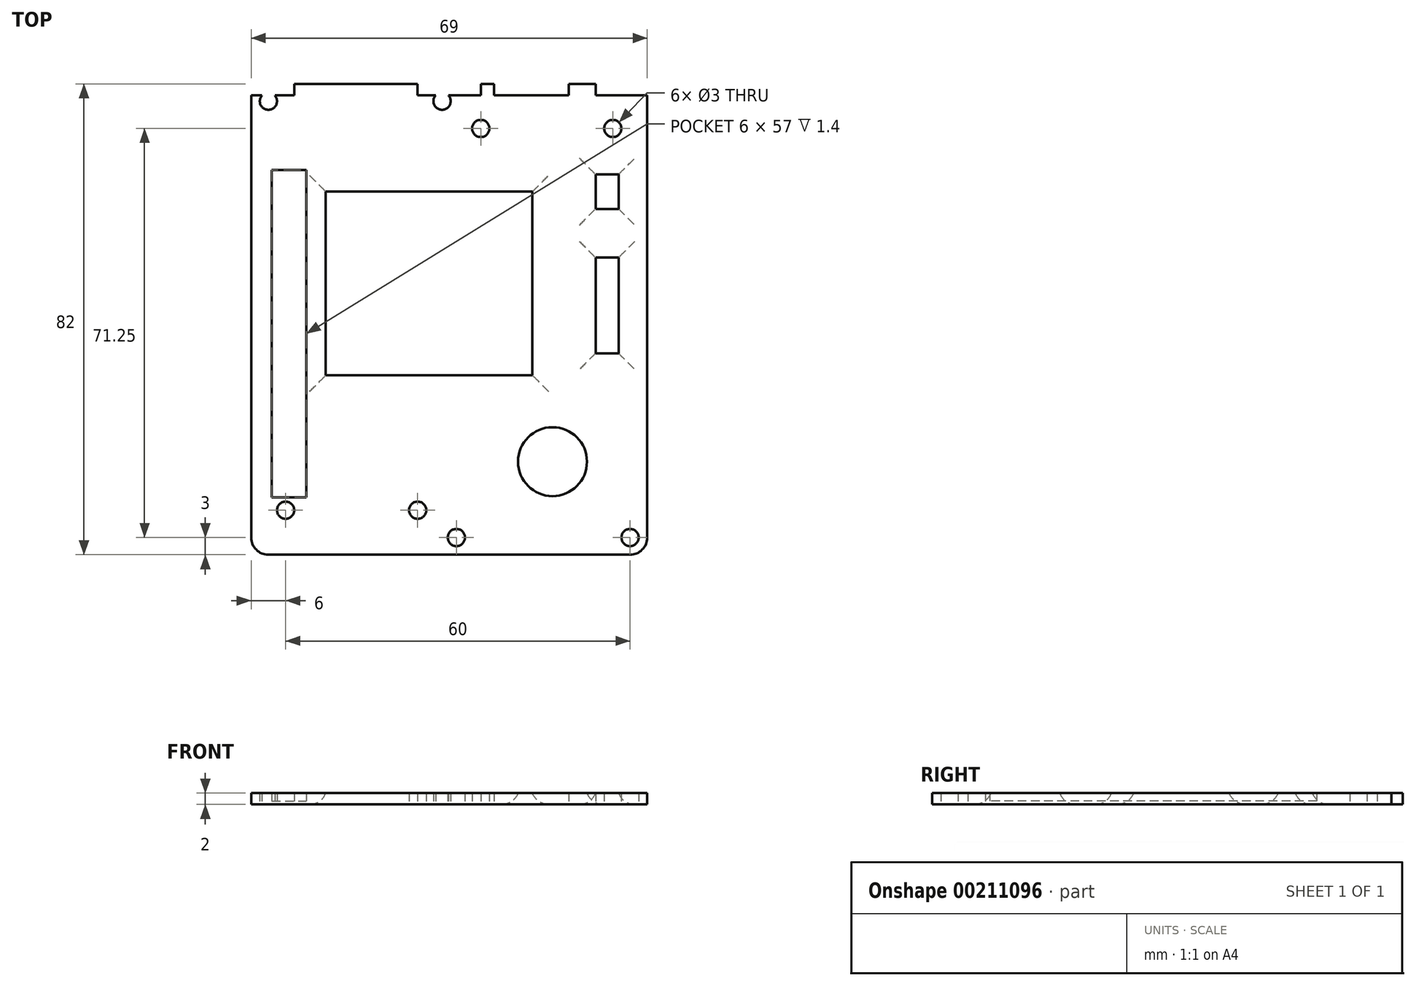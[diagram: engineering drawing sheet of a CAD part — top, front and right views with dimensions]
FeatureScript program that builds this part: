
annotation { "Feature Type Name" : "Feature", "Feature Type Description" : "" }
export const myFeature = defineFeature(function(context is Context, id is Id, definition is map)
    precondition{}
    {
        {
            var Q0;
            Q0=qCreatedBy(makeId("Top.planeOp"),FACE);
            var sketch = newSketch(context, id + "F0", { "sketchPlane" : qUnion([Q0])});
            skLineSegment(sketch, "E0.bottom", {"start": v(34.5, -41) * mm, "end": v(-34.5, -41) * mm});
            skLineSegment(sketch, "E0.top", {"start": v(34.5, 41) * mm, "end": v(-34.5, 41) * mm});
            skLineSegment(sketch, "E0.left", {"start": v(34.5, -41) * mm, "end": v(34.5, 41) * mm});
            skLineSegment(sketch, "E0.right", {"start": v(-34.5, -41) * mm, "end": v(-34.5, 41) * mm});
            skPoint(sketch, "E0.middle", {"position": v(0, 0) * mm});
            skLineSegment(sketch, "E1", {"start": v(-34.5, 39) * mm, "end": v(34.5, 39) * mm});
            skCircle(sketch, "E2", {"center": v(-28.5, 33.25) * mm, "radius": 1.5 * mm});
            skCircle(sketch, "E3", {"center": v(-5.5, 33.25) * mm, "radius": 1.5 * mm});
            skCircle(sketch, "E4.MirrorC", {"center": v(5.5, 33.25) * mm, "radius": 1.5 * mm});
            skCircle(sketch, "E5.MirrorC", {"center": v(28.5, 33.25) * mm, "radius": 1.5 * mm});
            skLineSegment(sketch, "E6.bottom", {"start": v(-21.5, 22.25) * mm, "end": v(14.5, 22.25) * mm});
            skLineSegment(sketch, "E6.top", {"start": v(-21.5, -9.75) * mm, "end": v(14.5, -9.75) * mm});
            skLineSegment(sketch, "E6.left", {"start": v(-21.5, 22.25) * mm, "end": v(-21.5, -9.75) * mm});
            skLineSegment(sketch, "E6.right", {"start": v(14.5, 22.25) * mm, "end": v(14.5, -9.75) * mm});
            skLineSegment(sketch, "E7.bottom", {"start": v(25.5, 25.25) * mm, "end": v(29.5, 25.25) * mm});
            skLineSegment(sketch, "E7.top", {"start": v(25.5, 19.25) * mm, "end": v(29.5, 19.25) * mm});
            skLineSegment(sketch, "E7.left", {"start": v(25.5, 25.25) * mm, "end": v(25.5, 19.25) * mm});
            skLineSegment(sketch, "E7.right", {"start": v(29.5, 25.25) * mm, "end": v(29.5, 19.25) * mm});
            skLineSegment(sketch, "E8.bottom", {"start": v(29.5, 10.75) * mm, "end": v(25.5, 10.75) * mm});
            skLineSegment(sketch, "E8.top", {"start": v(29.5, -5.91) * mm, "end": v(25.5, -5.91) * mm});
            skLineSegment(sketch, "E8.left", {"start": v(29.5, 10.75) * mm, "end": v(29.5, -5.91) * mm});
            skLineSegment(sketch, "E8.right", {"start": v(25.5, 10.75) * mm, "end": v(25.5, -5.91) * mm});
            skLineSegment(sketch, "E9.bottom", {"start": v(-5.5, 41) * mm, "end": v(5.5, 41) * mm});
            skLineSegment(sketch, "E9.top", {"start": v(-5.5, 39) * mm, "end": v(5.5, 39) * mm});
            skLineSegment(sketch, "E9.left", {"start": v(-5.5, 41) * mm, "end": v(-5.5, 39) * mm});
            skLineSegment(sketch, "E9.right", {"start": v(5.5, 41) * mm, "end": v(5.5, 39) * mm});
            skLineSegment(sketch, "E10.bottom", {"start": v(28.5, 39) * mm, "end": v(34.5, 39) * mm});
            skLineSegment(sketch, "E10.top", {"start": v(28, 41) * mm, "end": v(34.5, 41) * mm});
            skLineSegment(sketch, "E10.right", {"start": v(34.5, 39) * mm, "end": v(34.5, 41) * mm});
            skLineSegment(sketch, "E11.bottom", {"start": v(-28.5, 39) * mm, "end": v(-34.5, 39) * mm});
            skLineSegment(sketch, "E11.top", {"start": v(-27, 41) * mm, "end": v(-34.5, 41) * mm});
            skLineSegment(sketch, "E11.right", {"start": v(-34.5, 39) * mm, "end": v(-34.5, 41) * mm});
            skLineSegment(sketch, "E12", {"start": v(-25.5, 41) * mm, "end": v(-25.5, 39) * mm});
            skLineSegment(sketch, "E13.MirrorCS", {"start": v(25.5, 41) * mm, "end": v(25.5, 39) * mm});
            skLineSegment(sketch, "E14.bottom", {"start": v(-37, 41) * mm, "end": v(37, 41) * mm});
            skLineSegment(sketch, "E14.top", {"start": v(-37, -43.29) * mm, "end": v(37, -43.29) * mm});
            skLineSegment(sketch, "E14.left", {"start": v(-37, 41) * mm, "end": v(-37, -43.29) * mm});
            skLineSegment(sketch, "E14.right", {"start": v(37, 41) * mm, "end": v(37, -43.29) * mm});
            skLineSegment(sketch, "E15.bottom", {"start": v(-10.5, -43.29) * mm, "end": v(10.5, -43.29) * mm});
            skLineSegment(sketch, "E15.top", {"start": v(-10.5, -51.29) * mm, "end": v(10.5, -51.29) * mm});
            skLineSegment(sketch, "E15.left", {"start": v(-10.5, -43.29) * mm, "end": v(-10.5, -51.29) * mm});
            skLineSegment(sketch, "E15.right", {"start": v(10.5, -43.29) * mm, "end": v(10.5, -51.29) * mm});
            skLineSegment(sketch, "E16.bottom", {"start": v(-12.5, -41) * mm, "end": v(12.5, -41) * mm});
            skLineSegment(sketch, "E16.top", {"start": v(-12.5, -53.5) * mm, "end": v(12.5, -53.5) * mm});
            skLineSegment(sketch, "E16.left", {"start": v(-12.5, -41) * mm, "end": v(-12.5, -53.5) * mm});
            skLineSegment(sketch, "E16.right", {"start": v(12.5, -41) * mm, "end": v(12.5, -53.5) * mm});
            skLineSegment(sketch, "E17", {"start": v(-10.5, -43.29) * mm, "end": v(-10.5, -41) * mm});
            skLineSegment(sketch, "E18.MirrorCS", {"start": v(10.5, -43.29) * mm, "end": v(10.5, -41) * mm});
            skLineSegment(sketch, "E19.bottom", {"start": v(20.8, 41) * mm, "end": v(7.8, 41) * mm});
            skLineSegment(sketch, "E19.top", {"start": v(20.8, 39) * mm, "end": v(7.8, 39) * mm});
            skLineSegment(sketch, "E19.left", {"start": v(20.8, 41) * mm, "end": v(20.8, 39) * mm});
            skLineSegment(sketch, "E19.right", {"start": v(7.8, 41) * mm, "end": v(7.8, 39) * mm});
            skLineSegment(sketch, "E20", {"start": v(-14.5, 41) * mm, "end": v(-14.5, 39) * mm});
            skLineSegment(sketch, "E21", {"start": v(-27, 41) * mm, "end": v(-27, 39) * mm});
            skLineSegment(sketch, "E22.top", {"start": v(-37, 43) * mm, "end": v(37, 43) * mm});
            skLineSegment(sketch, "E22.left", {"start": v(-37, 41) * mm, "end": v(-37, 43) * mm});
            skLineSegment(sketch, "E22.right", {"start": v(37, 41) * mm, "end": v(37, 43) * mm});
            skCircle(sketch, "E23", {"center": v(-28.5, -33.25) * mm, "radius": 1.5 * mm});
            skCircle(sketch, "E24", {"center": v(-5.5, -33.25) * mm, "radius": 1.5 * mm});
            skCircle(sketch, "E25", {"center": v(18, -24.79) * mm, "radius": 6 * mm});
            skLineSegment(sketch, "E26.bottom", {"start": v(-30.9, 26) * mm, "end": v(-24.9, 26) * mm});
            skLineSegment(sketch, "E26.top", {"start": v(-30.9, -31) * mm, "end": v(-24.9, -31) * mm});
            skLineSegment(sketch, "E26.left", {"start": v(-30.9, 26) * mm, "end": v(-30.9, -31) * mm});
            skLineSegment(sketch, "E26.right", {"start": v(-24.9, 26) * mm, "end": v(-24.9, -31) * mm});
            skCircle(sketch, "E27", {"center": v(1.25, -38) * mm, "radius": 1.5 * mm});
            skCircle(sketch, "E28", {"center": v(31.5, -38) * mm, "radius": 1.5 * mm});
            skCircle(sketch, "E29", {"center": v(-1.25, 38) * mm, "radius": 1.5 * mm});
            skCircle(sketch, "E30", {"center": v(-31.5, 38) * mm, "radius": 1.5 * mm});
            skPoint(sketch, "E30.centerSnap0", {"position": v(-31.5, 39) * mm});
            skSolve(sketch);
        }
        {
            var Q0;
            {var subQ2=sQuery(id+"F0.wireOp",EDGE,"E0.bottom");Q0=makeQuery(id+"F0.imprint","IMPRINT",FACE,{"disambiguationData":[TD([[makeQuery(id+"F0.imprint","IMPRINT",EDGE,{"derivedFrom":subQ2}),-1.0]])]});}
            var Q1;
            {var subQ2=sQuery(id+"F0.wireOp",EDGE,"E11.bottom");Q1=makeQuery(id+"F0.imprint","IMPRINT",FACE,{"disambiguationData":[TD([[makeQuery(id+"F0.imprint","IMPRINT",EDGE,{"derivedFrom":subQ2}),-1.0]])]});}
            var Q2;
            {var subQ0=sQuery(id+"F0.wireOp",EDGE,"E12");Q2=makeQuery(id+"F0.imprint","IMPRINT",FACE,{"disambiguationData":[TD([[makeQuery(id+"F0.imprint","IMPRINT",EDGE,{"derivedFrom":subQ0}),-1.0]])]});}
            var Q3;
            {var subQ0=sQuery(id+"F0.wireOp",EDGE,"E12");Q3=makeQuery(id+"F0.imprint","IMPRINT",FACE,{"disambiguationData":[TD([[makeQuery(id+"F0.imprint","IMPRINT",EDGE,{"derivedFrom":subQ0}),1.0]])]});}
            var Q4;
            {var subQ0=sQuery(id+"F0.wireOp",EDGE,"E9.left");Q4=makeQuery(id+"F0.imprint","IMPRINT",FACE,{"disambiguationData":[TD([[makeQuery(id+"F0.imprint","IMPRINT",EDGE,{"derivedFrom":subQ0}),-1.0]])]});}
            var Q5;
            Q5=makeQuery(id+"F0.imprint","IMPRINT",FACE,{"disambiguationData":[TD([[makeQuery(id+"F0.imprint","IMPRINT",EDGE,{"derivedFrom":sQuery(id+"F0.wireOp",EDGE,"E9.top")}),1.0]])]});
            var Q6;
            {var subQ0=sQuery(id+"F0.wireOp",EDGE,"E9.right");Q6=makeQuery(id+"F0.imprint","IMPRINT",FACE,{"disambiguationData":[TD([[makeQuery(id+"F0.imprint","IMPRINT",EDGE,{"derivedFrom":subQ0}),1.0]])]});}
            var Q7;
            Q7=makeQuery(id+"F0.imprint","IMPRINT",FACE,{"disambiguationData":[TD([[makeQuery(id+"F0.imprint","IMPRINT",EDGE,{"derivedFrom":sQuery(id+"F0.wireOp",EDGE,"E19.top")}),-1.0]])]});
            var Q8;
            {var subQ0=sQuery(id+"F0.wireOp",EDGE,"E13.MirrorCS");Q8=makeQuery(id+"F0.imprint","IMPRINT",FACE,{"disambiguationData":[TD([[makeQuery(id+"F0.imprint","IMPRINT",EDGE,{"derivedFrom":subQ0}),-1.0]])]});}
            var Q9;
            {var subQ2=sQuery(id+"F0.wireOp",EDGE,"E10.bottom");Q9=makeQuery(id+"F0.imprint","IMPRINT",FACE,{"disambiguationData":[TD([[makeQuery(id+"F0.imprint","IMPRINT",EDGE,{"derivedFrom":subQ2}),1.0]])]});}
            var Q10;
            Q10=makeQuery(id+"F0.imprint","IMPRINT",FACE,{"disambiguationData":[TD([[makeQuery(id+"F0.imprint","IMPRINT",EDGE,{"derivedFrom":sQuery(id+"F0.wireOp",EDGE,"E3")}),1.0]])]});
            var Q11;
            Q11=makeQuery(id+"F0.imprint","IMPRINT",FACE,{"disambiguationData":[TD([[makeQuery(id+"F0.imprint","IMPRINT",EDGE,{"derivedFrom":sQuery(id+"F0.wireOp",EDGE,"E2")}),1.0]])]});
            extrude(context, id + "F1", {"entities" : qUnion([Q0, Q1, Q2, Q3, Q4, Q5, Q6, Q7, Q8, Q9, Q10, Q11]), "depth" : 2 * mm});
        }
        {
            var Q0;
            Q0=makeQuery(id+"F1.opExtrude","CAP_EDGE",EDGE,{"disambiguationData":[OSD([sQuery(id+"F0.wireOp",EDGE,"E8.right")])],"isStart":true});
            var Q1;
            Q1=makeQuery(id+"F1.opExtrude","CAP_EDGE",EDGE,{"disambiguationData":[OSD([sQuery(id+"F0.wireOp",EDGE,"E8.top")])],"isStart":true});
            var Q2;
            Q2=makeQuery(id+"F1.opExtrude","CAP_EDGE",EDGE,{"disambiguationData":[OSD([sQuery(id+"F0.wireOp",EDGE,"E8.left")])],"isStart":true});
            var Q3;
            Q3=makeQuery(id+"F1.opExtrude","CAP_EDGE",EDGE,{"disambiguationData":[OSD([sQuery(id+"F0.wireOp",EDGE,"E8.bottom")])],"isStart":true});
            var Q4;
            Q4=makeQuery(id+"F1.opExtrude","CAP_EDGE",EDGE,{"disambiguationData":[OSD([sQuery(id+"F0.wireOp",EDGE,"E7.top")])],"isStart":true});
            var Q5;
            Q5=makeQuery(id+"F1.opExtrude","CAP_EDGE",EDGE,{"disambiguationData":[OSD([sQuery(id+"F0.wireOp",EDGE,"E7.right")])],"isStart":true});
            var Q6;
            Q6=makeQuery(id+"F1.opExtrude","CAP_EDGE",EDGE,{"disambiguationData":[OSD([sQuery(id+"F0.wireOp",EDGE,"E7.bottom")])],"isStart":true});
            var Q7;
            Q7=makeQuery(id+"F1.opExtrude","CAP_EDGE",EDGE,{"disambiguationData":[OSD([sQuery(id+"F0.wireOp",EDGE,"E7.left")])],"isStart":true});
            var Q8;
            Q8=makeQuery(id+"F1.opExtrude","CAP_EDGE",EDGE,{"disambiguationData":[OSD([sQuery(id+"F0.wireOp",EDGE,"E6.right")])],"isStart":true});
            var Q9;
            Q9=makeQuery(id+"F1.opExtrude","CAP_EDGE",EDGE,{"disambiguationData":[OSD([sQuery(id+"F0.wireOp",EDGE,"E6.top")])],"isStart":true});
            var Q10;
            Q10=makeQuery(id+"F1.opExtrude","CAP_EDGE",EDGE,{"disambiguationData":[OSD([sQuery(id+"F0.wireOp",EDGE,"E6.bottom")])],"isStart":true});
            var Q11;
            Q11=makeQuery(id+"F1.opExtrude","CAP_EDGE",EDGE,{"disambiguationData":[OSD([sQuery(id+"F0.wireOp",EDGE,"E6.left")])],"isStart":true});
            var Q12;
            Q12=makeQuery(id+"F1.opExtrude","CAP_EDGE",EDGE,{"disambiguationData":[OSD([sQuery(id+"F0.wireOp",EDGE,"E25")])],"isStart":true});
            fillet(context, id + "F2", {"entities" : qUnion([Q0, Q1, Q2, Q3, Q4, Q5, Q6, Q7, Q8, Q9, Q10, Q11, Q12]), "radius" : 3 * mm, "tangentPropagation" : true, "allowEdgeOverflow" : false});
        }
        {
            var Q0;
            Q0=makeQuery(id+"F1.opExtrude","SWEPT_EDGE",EDGE,{"disambiguationData":[OSD([sQuery(id+"F0.wireOp",EDGE,"E11.right"),sQuery(id+"F0.wireOp",EDGE,"E14.bottom")])]});
            var Q1;
            Q1=makeQuery(id+"F1.opExtrude","SWEPT_EDGE",EDGE,{"disambiguationData":[OSD([sQuery(id+"F0.wireOp",EDGE,"E10.right"),sQuery(id+"F0.wireOp",EDGE,"E14.bottom")])]});
            var Q2;
            Q2=makeQuery(id+"F1.opExtrude","SWEPT_EDGE",EDGE,{"disambiguationData":[OSD([sQuery(id+"F0.wireOp",EDGE,"E0.bottom"),sQuery(id+"F0.wireOp",EDGE,"E0.left")])]});
            var Q3;
            Q3=makeQuery(id+"F1.opExtrude","SWEPT_EDGE",EDGE,{"disambiguationData":[OSD([sQuery(id+"F0.wireOp",EDGE,"E0.bottom"),sQuery(id+"F0.wireOp",EDGE,"E0.right")])]});
            fillet(context, id + "F3", {"entities" : qUnion([Q0, Q1, Q2, Q3]), "radius" : 3 * mm, "tangentPropagation" : true, "allowEdgeOverflow" : false});
        }
        {
            var Q0;
            Q0=makeQuery(id+"F0.imprint","IMPRINT",FACE,{"disambiguationData":[TD([[makeQuery(id+"F0.imprint","IMPRINT",EDGE,{"derivedFrom":sQuery(id+"F0.wireOp",EDGE,"E26.bottom")}),-1.0]])]});
            extrude(context, id + "F4", {"entities" : qUnion([Q0]), "operationType" : NewBodyOperationType.ADD, "depth" : .6 * mm});
        }
    });
